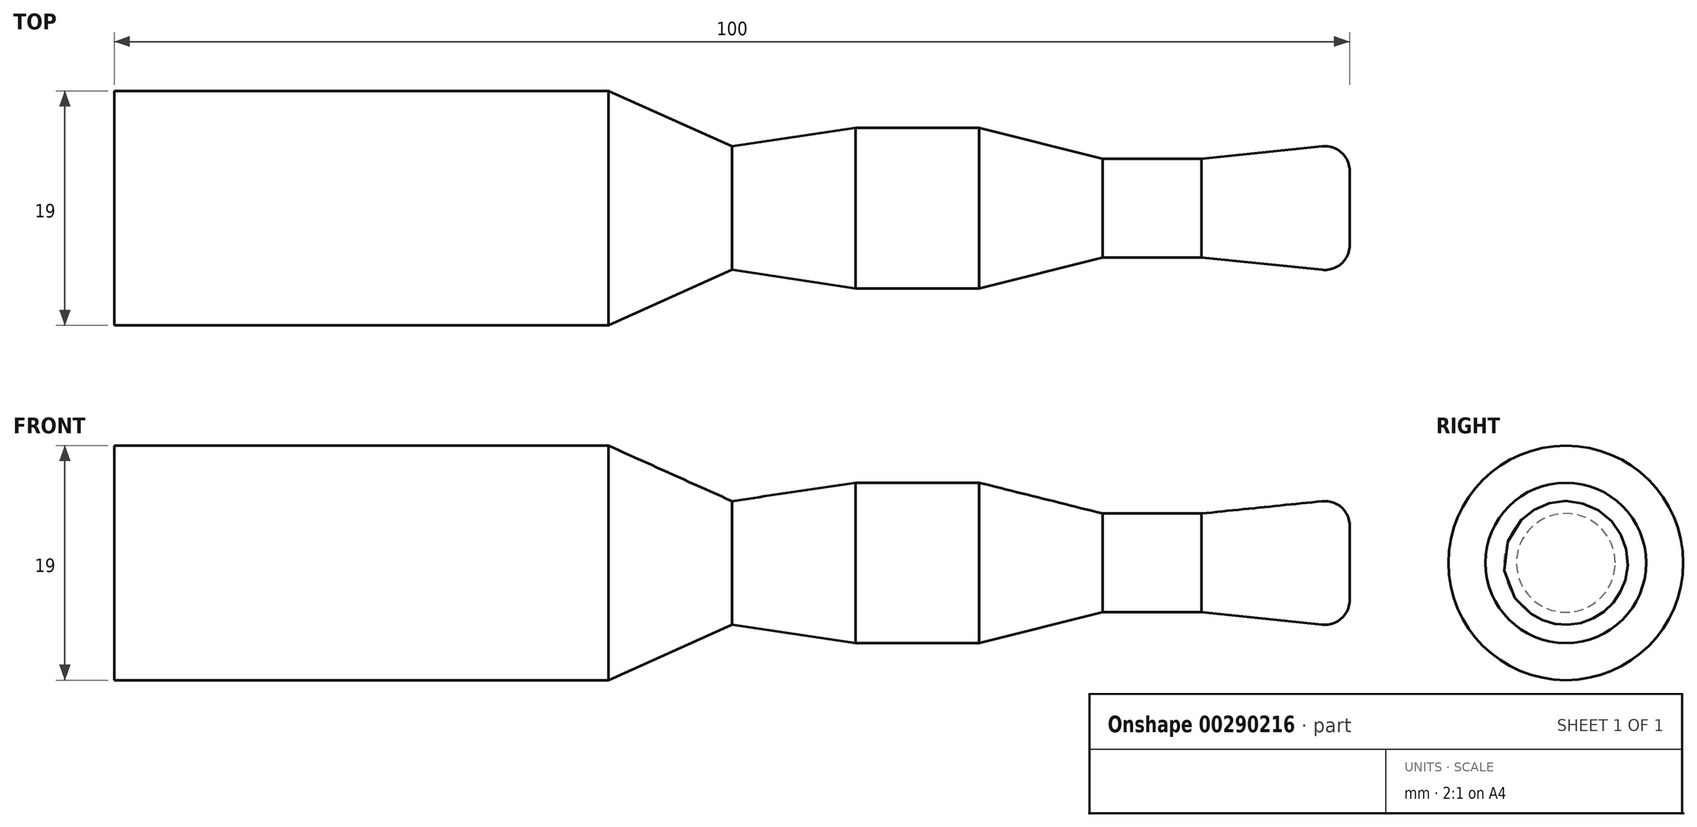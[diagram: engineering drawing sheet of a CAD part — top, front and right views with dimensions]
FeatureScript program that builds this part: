
annotation { "Feature Type Name" : "Feature", "Feature Type Description" : "" }
export const myFeature = defineFeature(function(context is Context, id is Id, definition is map)
    precondition{}
    {
        {
            var Q0;
            Q0=qCreatedBy(makeId("Front.planeOp"),FACE);
            var sketch = newSketch(context, id + "F0", { "sketchPlane" : qUnion([Q0])});
            skLineSegment(sketch, "E0", {"start": v(0, 0) * mm, "end": v(0, 3.01) * mm});
            skArc(sketch, "E1", {"start": v(0, 3.01) * mm, "mid": v(-0.66, 4.5) * mm, "end": v(-2.2, 5) * mm});
            skLineSegment(sketch, "E2", {"start": v(-2.2, 5) * mm, "end": v(-12, 4) * mm});
            skLineSegment(sketch, "E3", {"start": v(-30, 6.5) * mm, "end": v(-40, 6.5) * mm});
            skLineSegment(sketch, "E4", {"start": v(-40, 6.5) * mm, "end": v(-50, 5) * mm});
            skLineSegment(sketch, "E5", {"start": v(-50, 5) * mm, "end": v(-60, 9.5) * mm});
            skLineSegment(sketch, "E6", {"start": v(-60, 9.5) * mm, "end": v(-100, 9.5) * mm});
            skLineSegment(sketch, "E7", {"start": v(-100, 9.5) * mm, "end": v(-100, 0) * mm});
            skLineSegment(sketch, "E8", {"start": v(-100, 0) * mm, "end": v(0, 0) * mm});
            skLineSegment(sketch, "E9", {"start": v(-12, 4) * mm, "end": v(-20, 4) * mm});
            skLineSegment(sketch, "E10", {"start": v(-30, 6.5) * mm, "end": v(-20, 4) * mm});
            skSolve(sketch);
        }
        {
            var Q0;
            Q0 = qSketchRegion(id + "F0", true);
            var Q1;
            Q1=sQuery(id+"F0.wireOp",EDGE,"E8");
            revolve(context, id + "F1", {"entities" : qUnion([Q0]), "axis" : qUnion([Q1]), "revolveType" : RevolveType.FULL});
        }
    });
